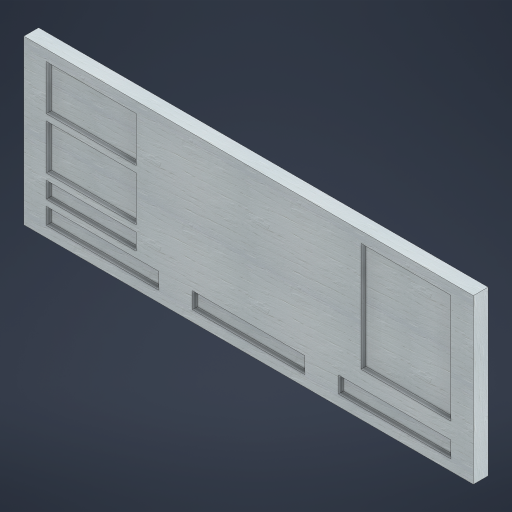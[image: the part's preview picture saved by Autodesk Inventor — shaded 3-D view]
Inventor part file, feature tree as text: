
AUTODESK INVENTOR PART (.ipt)
format: ipt  version: 2024 (Build 280153000, 153)  size: 425,472 bytes
history: native  units: mm
features: extrude x3, other x1, sketch x1
ambient origin geometry x8: Origin, YZ Plane, XZ Plane, XY Plane, X Axis, Y Axis, Z Axis, Center Point
bodies: Body1 (feature_tree)
feature tree (5):
  other  "Sólido1"
  extrude  "Extrusión1"  Depth=137.5mm
  extrude  "Extrusión2"  Depth=20.0mm
  extrude  "Extrusión3"  Depth=27.5mm
  sketch  "Boceto2"  dims[d3=0.0mm d4=137.5mm d5=20.0mm d6=27.5mm d7=137.5mm d8=20.0mm d9=27.5mm d10=13.333333mm d11=13.333333mm d12=137.5mm d13=41.25mm d14=41.25mm d15=20.0mm d17=110.0mm d18=133.333333mm d19=27.5mm d20=13.333333mm d21=110.0mm d22=55.0mm d23=27.5mm d24=13.333333mm d25=110.0mm d26=55.0mm d27=27.5mm d28=7.843137mm d29=110.0mm d30=20.0mm d31=7.843137mm d32=7.647059mm d33=6.0mm d34=0.0mm d35=9.0mm d36=9.0mm d37=9.0mm d38=9.0mm d39=9.0mm d40=66.666667mm d41=9.0mm d42=66.666667mm d43=9.0mm d44=66.666667mm d45=9.0mm d46=66.666667mm d47=6.0mm d48=0.0mm d49=0.5mm d50=0.872665mm d51=0.5mm d52=0.872665mm]
